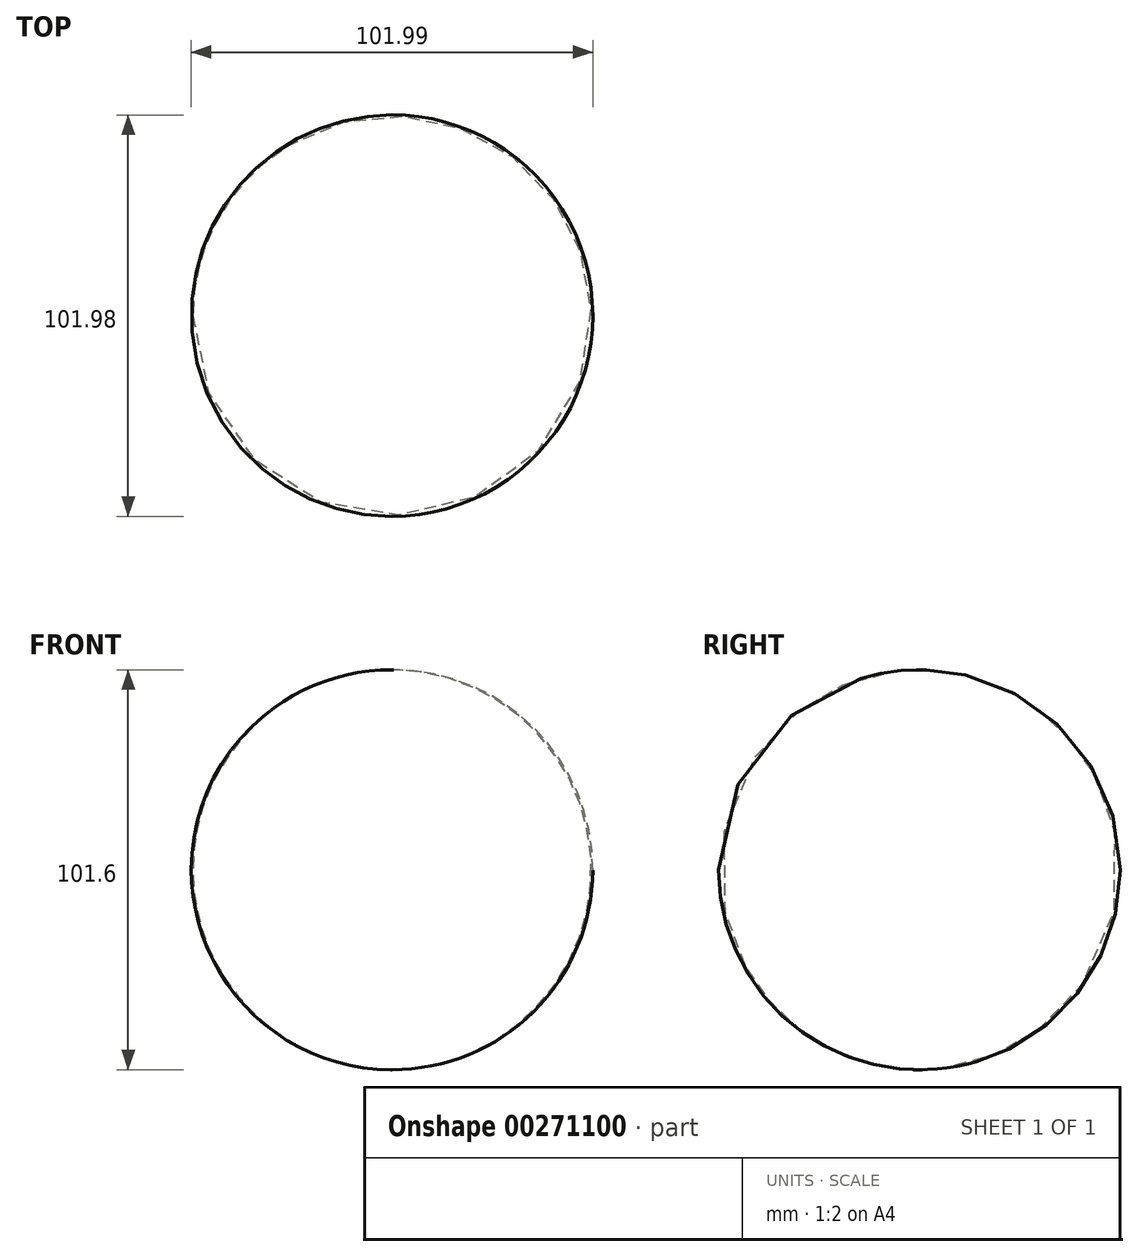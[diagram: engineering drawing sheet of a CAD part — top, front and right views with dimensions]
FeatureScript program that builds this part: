
annotation { "Feature Type Name" : "Feature", "Feature Type Description" : "" }
export const myFeature = defineFeature(function(context is Context, id is Id, definition is map)
    precondition{}
    {
        {
            var Q0;
            Q0=qCreatedBy(makeId("Front.planeOp"),FACE);
            var sketch = newSketch(context, id + "F0", { "sketchPlane" : qUnion([Q0])});
            skArc(sketch, "E0", {"start": v(0, 50.8) * mm, "mid": v(-50.8, 0.2) * mm, "end": v(-0.39, -50.8) * mm});
            skLineSegment(sketch, "E1", {"start": v(50.8, 0.2) * mm, "end": v(50.8, 0.2) * mm});
            skArc(sketch, "E2", {"start": v(50.8, 0) * mm, "mid": v(50.8, 0.1) * mm, "end": v(50.8, 0.2) * mm});
            skLineSegment(sketch, "E3", {"start": v(0, 50.8) * mm, "end": v(-0.39, -50.8) * mm});
            skSolve(sketch);
        }
        {
            var Q0;
            Q0 = qSketchRegion(id + "F0", true);
            var Q1;
            Q1=sQuery(id+"F0.wireOp",EDGE,"E3");
            revolve(context, id + "F1", {"entities" : qUnion([Q0]), "axis" : qUnion([Q1]), "revolveType" : RevolveType.FULL});
        }
    });
